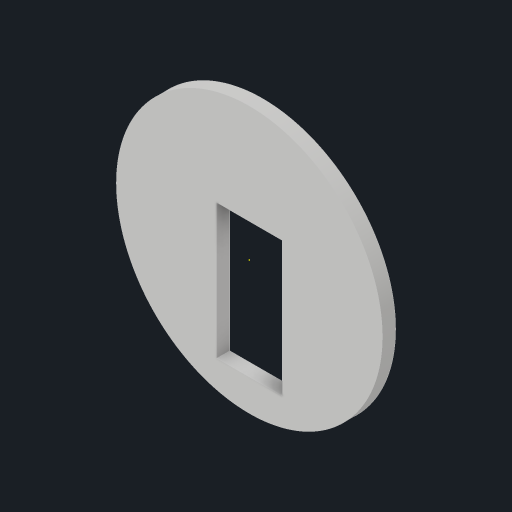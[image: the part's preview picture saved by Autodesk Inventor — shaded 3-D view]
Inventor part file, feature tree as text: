
AUTODESK INVENTOR PART (.ipt)
format: ipt  version: 2023.4 (Build 274418000, 418)  size: 230,400 bytes
history: native  units: in
note: dims shown in document units (in); Inventor stores cm internally (conversion verified against a paired STEP export)
features: extrude x2, sketch x2
ambient origin geometry x8: Origin, YZ Plane, XZ Plane, XY Plane, X Axis, Y Axis, Z Axis, Center Point
bodies: Solid1 (feature_tree)
feature tree (4):
  extrude  "Extrusion1"  Depth=0.4232in
  sketch  "Sketch5"  dims[d0=3.1496in d1=0.4232in]
  extrude  "Extrusion5"  Depth=0.7795in
  sketch  "Sketch7"  dims[d2=0.1575in d3=0.0in d19=0.7795in d20=1.5984in d21=0.3937in d22=0.3898in d23=0.1575in d24=0.0in]
